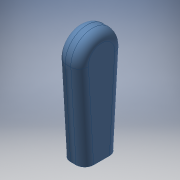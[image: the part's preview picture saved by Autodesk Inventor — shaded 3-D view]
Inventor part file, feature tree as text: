
AUTODESK INVENTOR PART (.ipt)
format: ipt  version: 2018.1 (Build 221151000, 151)  size: 143,872 bytes
history: native  units: in
note: dims shown in document units (in); Inventor stores cm internally (conversion verified against a paired STEP export)
features: extrude x2, sketch x1, fillet x1
ambient origin geometry x8: Origin, YZ Plane, XZ Plane, XY Plane, X Axis, Y Axis, Z Axis, Center Point
bodies: Solid2 (feature_tree)
feature tree (4):
  sketch  "Sketch1"  dims[d0=0.674in d2=0.4409in d3=0.087in d4=1.8406in d5=1.7795in d7=0.3346in d9=0.0094in d10=0.4646in d11=0.0in d12=0.1772in d13=0.2441in d14=0.0in]
  extrude  "Extrusion1"  Depth=0.4409in
  fillet  "Fillet1"  Radius=0.087in
  extrude  "Extrusion2"  Depth=0.2441in
